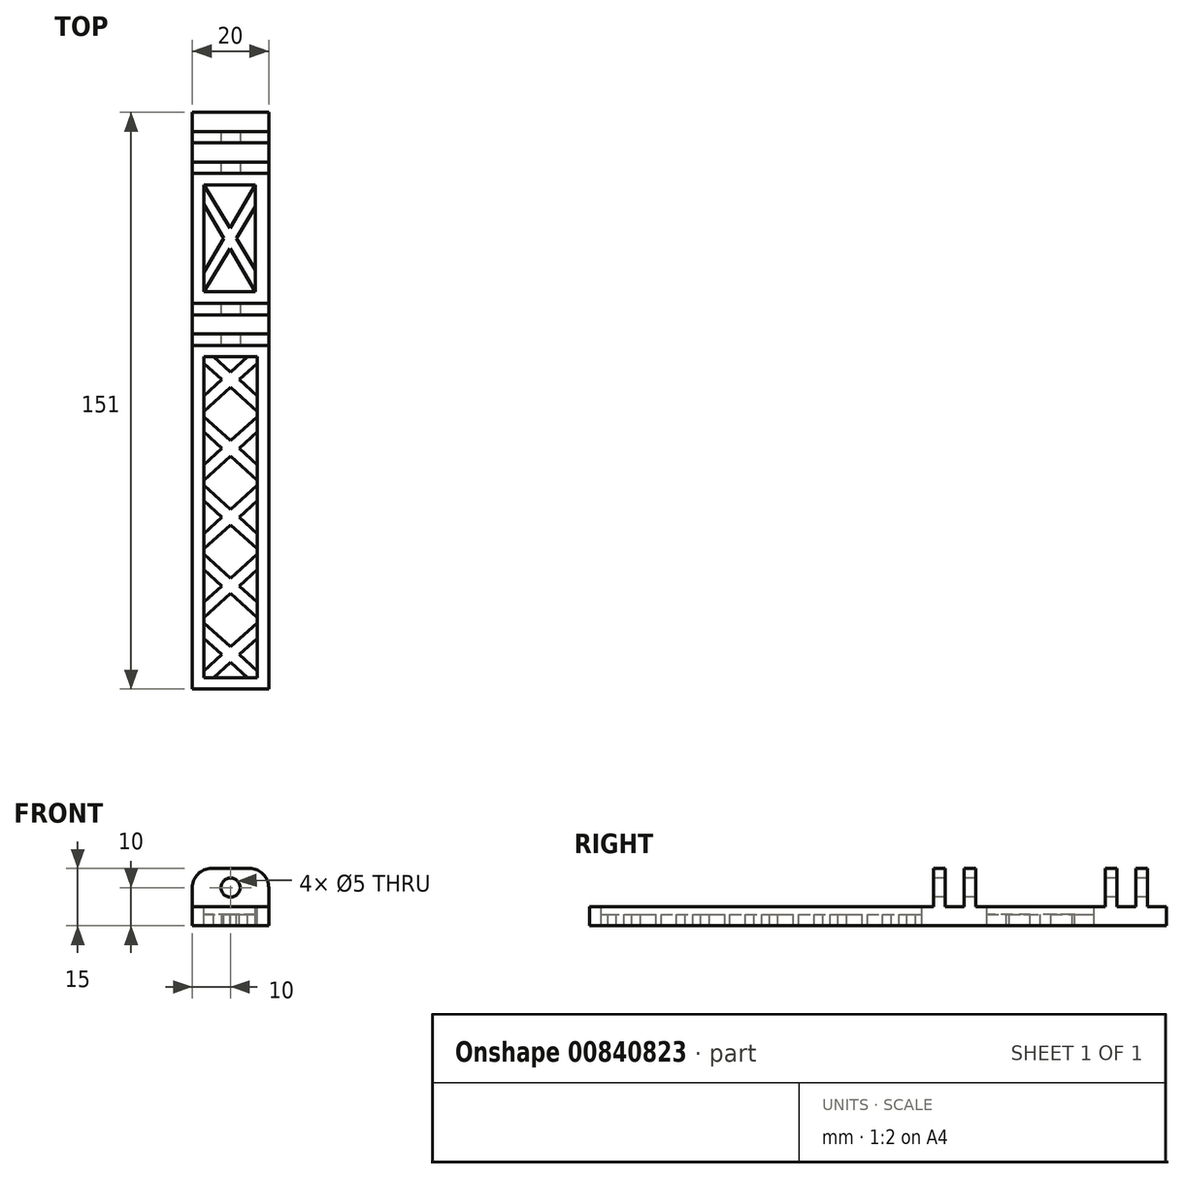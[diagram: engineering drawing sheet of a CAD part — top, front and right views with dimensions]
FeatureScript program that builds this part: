
annotation { "Feature Type Name" : "Feature", "Feature Type Description" : "" }
export const myFeature = defineFeature(function(context is Context, id is Id, definition is map)
    precondition{}
    {
        {
            var Q0;
            Q0=qCreatedBy(makeId("Top.planeOp"),FACE);
            var sketch = newSketch(context, id + "F0", { "sketchPlane" : qUnion([Q0])});
            skLineSegment(sketch, "E0.bottom", {"start": v(10, 75.5) * mm, "end": v(-10, 75.5) * mm});
            skLineSegment(sketch, "E0.top", {"start": v(10, -75.5) * mm, "end": v(-10, -75.5) * mm});
            skLineSegment(sketch, "E0.left", {"start": v(10, 75.5) * mm, "end": v(10, -75.5) * mm});
            skLineSegment(sketch, "E0.right", {"start": v(-10, 75.5) * mm, "end": v(-10, -75.5) * mm});
            skPoint(sketch, "E0.middle", {"position": v(0, 0) * mm});
            skLineSegment(sketch, "E1.bottom", {"start": v(-10, 70.5) * mm, "end": v(10, 70.5) * mm});
            skLineSegment(sketch, "E1.top", {"start": v(-10, 67.5) * mm, "end": v(10, 67.5) * mm});
            skLineSegment(sketch, "E1.left", {"start": v(-10, 70.5) * mm, "end": v(-10, 67.5) * mm});
            skLineSegment(sketch, "E1.right", {"start": v(10, 70.5) * mm, "end": v(10, 67.5) * mm});
            skLineSegment(sketch, "E2", {"start": v(-10, 62.5) * mm, "end": v(10, 62.5) * mm});
            skLineSegment(sketch, "E3", {"start": v(-10, 59.5) * mm, "end": v(10, 59.5) * mm});
            skLineSegment(sketch, "E4", {"start": v(-10, 22.5) * mm, "end": v(10, 22.5) * mm});
            skLineSegment(sketch, "E5", {"start": v(-10, 17.5) * mm, "end": v(10, 17.5) * mm});
            skLineSegment(sketch, "E6", {"start": v(-10, 25.5) * mm, "end": v(10, 25.5) * mm});
            skLineSegment(sketch, "E7", {"start": v(-10, 14.5) * mm, "end": v(10, 14.5) * mm});
            skSolve(sketch);
        }
        {
            var Q0;
            {var subQ0=sQuery(id+"F0.wireOp",EDGE,"E3");var subQ5=makeQuery(id+"F0.imprint","IMPRINT",EDGE,{"derivedFrom":subQ0});var subQ10=sQuery(id+"F0.wireOp",EDGE,"E1.top");var subQ12=sQuery(id+"F0.wireOp",EDGE,"E1.bottom");var subQ14=makeQuery(id+"F0.imprint","IMPRINT",EDGE,{"derivedFrom":subQ12});var subQ17=makeQuery(id+"F0.imprint","IMPRINT",EDGE,{"derivedFrom":subQ10});var subQ20=sQuery(id+"F0.wireOp",EDGE,"E5");var subQ25=makeQuery(id+"F0.imprint","IMPRINT",EDGE,{"derivedFrom":subQ20});var subQ26=sQuery(id+"F0.wireOp",EDGE,"E0.top");var subQ27=sQuery(id+"F0.wireOp",EDGE,"E4");var subQ29=makeQuery(id+"F0.imprint","IMPRINT",EDGE,{"derivedFrom":subQ27});var subQ31=sQuery(id+"F0.wireOp",EDGE,"E0.bottom");var subQ32=sQuery(id+"F0.wireOp",EDGE,"E2");var subQ35=makeQuery(id+"F0.imprint","IMPRINT",EDGE,{"derivedFrom":subQ32});Q0=qUnion([makeQuery(id+"F0.imprint","IMPRINT",FACE,{"disambiguationData":[TD([[subQ17,-1.0]])]}),makeQuery(id+"F0.imprint","IMPRINT",FACE,{"disambiguationData":[TD([[subQ35,-1.0]])]}),makeQuery(id+"F0.imprint","IMPRINT",FACE,{"disambiguationData":[TD([[makeQuery(id+"F0.imprint","IMPRINT",EDGE,{"derivedFrom":subQ31}),1.0]])]}),makeQuery(id+"F0.imprint","IMPRINT",FACE,{"disambiguationData":[TD([[subQ29,-1.0]])]}),makeQuery(id+"F0.imprint","IMPRINT",FACE,{"disambiguationData":[TD([[subQ29,1.0]])]}),makeQuery(id+"F0.imprint","IMPRINT",FACE,{"disambiguationData":[TD([[makeQuery(id+"F0.imprint","IMPRINT",EDGE,{"derivedFrom":subQ26}),-1.0]])]}),makeQuery(id+"F0.imprint","IMPRINT",FACE,{"disambiguationData":[TD([[subQ25,-1.0]])]}),makeQuery(id+"F0.imprint","IMPRINT",FACE,{"disambiguationData":[TD([[subQ14,-1.0]])]}),makeQuery(id+"F0.imprint","IMPRINT",FACE,{"disambiguationData":[TD([[subQ5,-1.0]])]})]);}
            extrude(context, id + "F1", {"entities" : qUnion([Q0]), "depth" : 5 * mm, "offsetDistance" : 25 * mm});
        }
        {
            var Q0;
            Q0=qCreatedBy(makeId("Top.planeOp"),FACE);
            var sketch = newSketch(context, id + "F2", { "sketchPlane" : qUnion([Q0])});
            skLineSegment(sketch, "E8.0", {"start": v(-10, 70.5) * mm, "end": v(10, 70.5) * mm});
            skLineSegment(sketch, "E9.0", {"start": v(-10, 67.5) * mm, "end": v(10, 67.5) * mm});
            skLineSegment(sketch, "E10.0", {"start": v(-10, 62.5) * mm, "end": v(10, 62.5) * mm});
            skLineSegment(sketch, "E11.0", {"start": v(-10, 59.5) * mm, "end": v(10, 59.5) * mm});
            skLineSegment(sketch, "E12.0", {"start": v(-10, 25.5) * mm, "end": v(10, 25.5) * mm});
            skLineSegment(sketch, "E13.0", {"start": v(-10, 22.5) * mm, "end": v(10, 22.5) * mm});
            skLineSegment(sketch, "E14.0", {"start": v(-10, 17.5) * mm, "end": v(10, 17.5) * mm});
            skLineSegment(sketch, "E15.0", {"start": v(-10, 14.5) * mm, "end": v(10, 14.5) * mm});
            skLineSegment(sketch, "E16.0", {"start": v(-10, 75.5) * mm, "end": v(-10, -75.5) * mm});
            skLineSegment(sketch, "E17.0", {"start": v(10, 75.5) * mm, "end": v(10, -75.5) * mm});
            skLineSegment(sketch, "E18.0.1", {"start": v(-10, -75.5) * mm, "end": v(10, -75.5) * mm});
            skLineSegment(sketch, "E18.0.2", {"start": v(10, -75.5) * mm, "end": v(10, 75.5) * mm});
            skLineSegment(sketch, "E18.0.3", {"start": v(10, 75.5) * mm, "end": v(-10, 75.5) * mm});
            skSolve(sketch);
        }
        {
            var Q0;
            {var subQ0=sQuery(id+"F2.wireOp",EDGE,"E8.0");var subQ1=sQuery(id+"F2.wireOp",EDGE,"E16.0");var subQ2=makeQuery(id+"F2.imprint","INTERSECT",VERTEX,{"derivedFrom":[subQ1,subQ0]});Q0=makeQuery(id+"F2.imprint","IMPRINT",FACE,{"disambiguationData":[TD([[makeQuery(id+"F2.imprint","IMPRINT",EDGE,{"disambiguationData":[TD([[subQ2,-1.0]])],"derivedFrom":subQ1}),1.0]])]});}
            var Q1;
            {var subQ0=sQuery(id+"F2.wireOp",EDGE,"E8.0");Q1=makeQuery(id+"F2.imprint","IMPRINT",FACE,{"disambiguationData":[TD([[makeQuery(id+"F2.imprint","IMPRINT",EDGE,{"derivedFrom":subQ0}),-1.0]])]});}
            var Q2;
            {var subQ0=sQuery(id+"F2.wireOp",EDGE,"E8.0");var subQ1=sQuery(id+"F2.wireOp",EDGE,"E18.0.2");var subQ2=makeQuery(id+"F2.imprint","INTERSECT",VERTEX,{"derivedFrom":[subQ1,subQ0]});Q2=makeQuery(id+"F2.imprint","IMPRINT",FACE,{"disambiguationData":[TD([[makeQuery(id+"F2.imprint","IMPRINT",EDGE,{"disambiguationData":[TD([[subQ2,-1.0]])],"derivedFrom":subQ1}),-1.0]])]});}
            var Q3;
            {var subQ0=sQuery(id+"F2.wireOp",EDGE,"E10.0");var subQ1=sQuery(id+"F2.wireOp",EDGE,"E18.0.2");var subQ2=makeQuery(id+"F2.imprint","INTERSECT",VERTEX,{"derivedFrom":[subQ1,subQ0]});Q3=makeQuery(id+"F2.imprint","IMPRINT",FACE,{"disambiguationData":[TD([[makeQuery(id+"F2.imprint","IMPRINT",EDGE,{"disambiguationData":[TD([[subQ2,-1.0]])],"derivedFrom":subQ1}),-1.0]])]});}
            var Q4;
            {var subQ0=sQuery(id+"F2.wireOp",EDGE,"E10.0");Q4=makeQuery(id+"F2.imprint","IMPRINT",FACE,{"disambiguationData":[TD([[makeQuery(id+"F2.imprint","IMPRINT",EDGE,{"derivedFrom":subQ0}),-1.0]])]});}
            var Q5;
            {var subQ0=sQuery(id+"F2.wireOp",EDGE,"E10.0");var subQ1=sQuery(id+"F2.wireOp",EDGE,"E16.0");var subQ2=makeQuery(id+"F2.imprint","INTERSECT",VERTEX,{"derivedFrom":[subQ1,subQ0]});Q5=makeQuery(id+"F2.imprint","IMPRINT",FACE,{"disambiguationData":[TD([[makeQuery(id+"F2.imprint","IMPRINT",EDGE,{"disambiguationData":[TD([[subQ2,-1.0]])],"derivedFrom":subQ1}),1.0]])]});}
            var Q6;
            {var subQ0=sQuery(id+"F2.wireOp",EDGE,"E12.0");var subQ1=sQuery(id+"F2.wireOp",EDGE,"E16.0");var subQ2=makeQuery(id+"F2.imprint","INTERSECT",VERTEX,{"derivedFrom":[subQ1,subQ0]});Q6=makeQuery(id+"F2.imprint","IMPRINT",FACE,{"disambiguationData":[TD([[makeQuery(id+"F2.imprint","IMPRINT",EDGE,{"disambiguationData":[TD([[subQ2,-1.0]])],"derivedFrom":subQ1}),1.0]])]});}
            var Q7;
            {var subQ0=sQuery(id+"F2.wireOp",EDGE,"E12.0");Q7=makeQuery(id+"F2.imprint","IMPRINT",FACE,{"disambiguationData":[TD([[makeQuery(id+"F2.imprint","IMPRINT",EDGE,{"derivedFrom":subQ0}),-1.0]])]});}
            var Q8;
            {var subQ0=sQuery(id+"F2.wireOp",EDGE,"E12.0");var subQ1=sQuery(id+"F2.wireOp",EDGE,"E18.0.2");var subQ2=makeQuery(id+"F2.imprint","INTERSECT",VERTEX,{"derivedFrom":[subQ1,subQ0]});Q8=makeQuery(id+"F2.imprint","IMPRINT",FACE,{"disambiguationData":[TD([[makeQuery(id+"F2.imprint","IMPRINT",EDGE,{"disambiguationData":[TD([[subQ2,-1.0]])],"derivedFrom":subQ1}),-1.0]])]});}
            var Q9;
            {var subQ0=sQuery(id+"F2.wireOp",EDGE,"E14.0");var subQ1=sQuery(id+"F2.wireOp",EDGE,"E18.0.2");var subQ2=makeQuery(id+"F2.imprint","INTERSECT",VERTEX,{"derivedFrom":[subQ1,subQ0]});Q9=makeQuery(id+"F2.imprint","IMPRINT",FACE,{"disambiguationData":[TD([[makeQuery(id+"F2.imprint","IMPRINT",EDGE,{"disambiguationData":[TD([[subQ2,-1.0]])],"derivedFrom":subQ1}),-1.0]])]});}
            var Q10;
            {var subQ0=sQuery(id+"F2.wireOp",EDGE,"E14.0");Q10=makeQuery(id+"F2.imprint","IMPRINT",FACE,{"disambiguationData":[TD([[makeQuery(id+"F2.imprint","IMPRINT",EDGE,{"derivedFrom":subQ0}),-1.0]])]});}
            var Q11;
            {var subQ0=sQuery(id+"F2.wireOp",EDGE,"E14.0");var subQ1=sQuery(id+"F2.wireOp",EDGE,"E16.0");var subQ2=makeQuery(id+"F2.imprint","INTERSECT",VERTEX,{"derivedFrom":[subQ1,subQ0]});Q11=makeQuery(id+"F2.imprint","IMPRINT",FACE,{"disambiguationData":[TD([[makeQuery(id+"F2.imprint","IMPRINT",EDGE,{"disambiguationData":[TD([[subQ2,-1.0]])],"derivedFrom":subQ1}),1.0]])]});}
            var Q12;
            Q12=makeQuery(id+"F1.opExtrude","CAP_FACE",FACE,{"disambiguationData":[OSD([sQuery(id+"F0.wireOp",EDGE,"E0.bottom"),sQuery(id+"F0.wireOp",EDGE,"E0.top"),sQuery(id+"F0.wireOp",EDGE,"E0.left"),sQuery(id+"F0.wireOp",EDGE,"E0.right")])],"isStart":false});
            extrude(context, id + "F3", {"entities" : qUnion([Q0, Q1, Q2, Q3, Q4, Q5, Q6, Q7, Q8, Q9, Q10, Q11]), "operationType" : NewBodyOperationType.ADD, "endBound" : BoundingType.UP_TO_SURFACE, "depth" : 10 * mm, "endBoundEntityFace" : qUnion([Q12]), "offsetDistance" : 25 * mm});
        }
        {
            var Q0;
            Q0=makeQuery(id+"F1.opExtrude","CAP_FACE",FACE,{"disambiguationData":[OSD([sQuery(id+"F0.wireOp",EDGE,"E0.bottom"),sQuery(id+"F0.wireOp",EDGE,"E0.top"),sQuery(id+"F0.wireOp",EDGE,"E0.left"),sQuery(id+"F0.wireOp",EDGE,"E0.right")])],"isStart":false});
            var sketch = newSketch(context, id + "F4", { "sketchPlane" : qUnion([Q0])});
            skPoint(sketch, "E19.0", {"position": v(-10, 70.5) * mm});
            skPoint(sketch, "E20.0", {"position": v(10, 67.5) * mm});
            skPoint(sketch, "E21.0", {"position": v(10, 62.5) * mm});
            skPoint(sketch, "E22.0", {"position": v(-10, 59.5) * mm});
            skPoint(sketch, "E23.0", {"position": v(-10, 25.5) * mm});
            skPoint(sketch, "E24.0", {"position": v(10, 22.5) * mm});
            skPoint(sketch, "E25.0", {"position": v(10, 17.5) * mm});
            skPoint(sketch, "E26.0", {"position": v(-10, 14.5) * mm});
            skLineSegment(sketch, "E27.bottom", {"start": v(-10, 70.5) * mm, "end": v(10, 70.5) * mm});
            skLineSegment(sketch, "E27.top", {"start": v(-10, 67.5) * mm, "end": v(10, 67.5) * mm});
            skLineSegment(sketch, "E27.left", {"start": v(-10, 70.5) * mm, "end": v(-10, 67.5) * mm});
            skLineSegment(sketch, "E27.right", {"start": v(10, 70.5) * mm, "end": v(10, 67.5) * mm});
            skLineSegment(sketch, "E28.bottom", {"start": v(10, 62.5) * mm, "end": v(-10, 62.5) * mm});
            skLineSegment(sketch, "E28.top", {"start": v(10, 59.5) * mm, "end": v(-10, 59.5) * mm});
            skLineSegment(sketch, "E28.left", {"start": v(10, 62.5) * mm, "end": v(10, 59.5) * mm});
            skLineSegment(sketch, "E28.right", {"start": v(-10, 62.5) * mm, "end": v(-10, 59.5) * mm});
            skLineSegment(sketch, "E29.bottom", {"start": v(-10, 25.5) * mm, "end": v(10, 25.5) * mm});
            skLineSegment(sketch, "E29.top", {"start": v(-10, 22.5) * mm, "end": v(10, 22.5) * mm});
            skLineSegment(sketch, "E29.left", {"start": v(-10, 25.5) * mm, "end": v(-10, 22.5) * mm});
            skLineSegment(sketch, "E29.right", {"start": v(10, 25.5) * mm, "end": v(10, 22.5) * mm});
            skLineSegment(sketch, "E30.bottom", {"start": v(10, 17.5) * mm, "end": v(-10, 17.5) * mm});
            skLineSegment(sketch, "E30.top", {"start": v(10, 14.5) * mm, "end": v(-10, 14.5) * mm});
            skLineSegment(sketch, "E30.left", {"start": v(10, 17.5) * mm, "end": v(10, 14.5) * mm});
            skLineSegment(sketch, "E30.right", {"start": v(-10, 17.5) * mm, "end": v(-10, 14.5) * mm});
            skSolve(sketch);
        }
        {
            var Q0;
            Q0 = qSketchRegion(id + "F4", true);
            extrude(context, id + "F5", {"entities" : qUnion([Q0]), "operationType" : NewBodyOperationType.ADD, "depth" : 10 * mm, "offsetDistance" : 25 * mm});
        }
        {
            var Q0;
            Q0=makeQuery(id+"F5.opExtrude","SWEPT_FACE",FACE,{"disambiguationData":[OSD([sQuery(id+"F4.wireOp",EDGE,"E30.top")])]});
            var sketch = newSketch(context, id + "F6", { "sketchPlane" : qUnion([Q0])});
            skCircle(sketch, "E31", {"center": v(0, 10) * mm, "radius": 2.5 * mm});
            skPoint(sketch, "E32", {"position": v(0, 15) * mm});
            skPoint(sketch, "E33", {"position": v(-10, 10) * mm});
            skSolve(sketch);
        }
        {
            var Q0;
            Q0=makeQuery(id+"F6.imprint","IMPRINT",FACE,{"disambiguationData":[TD([[makeQuery(id+"F6.imprint","IMPRINT",EDGE,{"derivedFrom":sQuery(id+"F6.wireOp",EDGE,"E31")}),1.0]])]});
            var Q1;
            Q1=makeQuery(id+"F5.opExtrude","SWEPT_FACE",FACE,{"disambiguationData":[OSD([sQuery(id+"F4.wireOp",EDGE,"E27.bottom")])]});
            extrude(context, id + "F7", {"entities" : qUnion([Q0]), "operationType" : NewBodyOperationType.REMOVE, "endBound" : BoundingType.UP_TO_SURFACE, "oppositeDirection" : true, "depth" : 25 * mm, "endBoundEntityFace" : qUnion([Q1]), "offsetDistance" : 25 * mm});
        }
        {
            var Q0;
            Q0=makeQuery(id+"F5.opExtrude","CAP_EDGE",EDGE,{"disambiguationData":[OSD([sQuery(id+"F4.wireOp",EDGE,"E27.right")])],"isStart":false});
            var Q1;
            Q1=makeQuery(id+"F5.opExtrude","CAP_EDGE",EDGE,{"disambiguationData":[OSD([sQuery(id+"F4.wireOp",EDGE,"E28.left")])],"isStart":false});
            var Q2;
            Q2=makeQuery(id+"F5.opExtrude","CAP_EDGE",EDGE,{"disambiguationData":[OSD([sQuery(id+"F4.wireOp",EDGE,"E28.right")])],"isStart":false});
            var Q3;
            Q3=makeQuery(id+"F5.opExtrude","CAP_EDGE",EDGE,{"disambiguationData":[OSD([sQuery(id+"F4.wireOp",EDGE,"E27.left")])],"isStart":false});
            var Q4;
            Q4=makeQuery(id+"F5.opExtrude","CAP_EDGE",EDGE,{"disambiguationData":[OSD([sQuery(id+"F4.wireOp",EDGE,"E29.right")])],"isStart":false});
            var Q5;
            Q5=makeQuery(id+"F5.opExtrude","CAP_EDGE",EDGE,{"disambiguationData":[OSD([sQuery(id+"F4.wireOp",EDGE,"E29.left")])],"isStart":false});
            var Q6;
            Q6=makeQuery(id+"F5.opExtrude","CAP_EDGE",EDGE,{"disambiguationData":[OSD([sQuery(id+"F4.wireOp",EDGE,"E30.right")])],"isStart":false});
            var Q7;
            Q7=makeQuery(id+"F5.opExtrude","CAP_EDGE",EDGE,{"disambiguationData":[OSD([sQuery(id+"F4.wireOp",EDGE,"E30.left")])],"isStart":false});
            fillet(context, id + "F8", {"entities" : qUnion([Q0, Q1, Q2, Q3, Q4, Q5, Q6, Q7]), "radius" : 5 * mm, "tangentPropagation" : true, "allowEdgeOverflow" : false});
        }
        {
            var Q0;
            {var subQ0=sQuery(id+"F0.wireOp",EDGE,"E0.right");var subQ1=sQuery(id+"F0.wireOp",EDGE,"E0.top");var subQ2=sQuery(id+"F0.wireOp",EDGE,"E0.left");Q0=makeQuery(id+"F5.boolean.opBoolean","SPLIT",FACE,{"disambiguationData":[TD([makeQuery(id+"F1.opExtrude","SWEPT_FACE",FACE,{"disambiguationData":[OSD([subQ1])]})])],"derivedFrom":makeQuery(id+"F1.opExtrude","CAP_FACE",FACE,{"disambiguationData":[OSD([sQuery(id+"F0.wireOp",EDGE,"E0.bottom"),subQ1,subQ2,subQ0])],"isStart":false})});}
            var sketch = newSketch(context, id + "F9", { "sketchPlane" : qUnion([Q0])});
            skLineSegment(sketch, "E34.bottom", {"start": v(-10, 14.5) * mm, "end": v(10, 14.5) * mm});
            skLineSegment(sketch, "E34.top", {"start": v(-10, -75.5) * mm, "end": v(10, -75.5) * mm});
            skLineSegment(sketch, "E34.left", {"start": v(-10, 14.5) * mm, "end": v(-10, -75.5) * mm});
            skLineSegment(sketch, "E34.right", {"start": v(10, 14.5) * mm, "end": v(10, -75.5) * mm});
            skLineSegment(sketch, "E35", {"start": v(-10, 14.5) * mm, "end": v(10, -3.5) * mm, "construction": true});
            skLineSegment(sketch, "E36", {"start": v(10, -3.5) * mm, "end": v(-10, -21.5) * mm, "construction": true});
            skLineSegment(sketch, "E37", {"start": v(-10, -21.5) * mm, "end": v(10, -39.5) * mm, "construction": true});
            skLineSegment(sketch, "E38", {"start": v(10, -39.5) * mm, "end": v(-10, -57.5) * mm, "construction": true});
            skLineSegment(sketch, "E39", {"start": v(-10, -57.5) * mm, "end": v(10, -75.5) * mm, "construction": true});
            skLineSegment(sketch, "E40.0", {"start": v(-11, 13.39) * mm, "end": v(9, -4.61) * mm});
            skLineSegment(sketch, "E41.MirrorCS", {"start": v(-9, 15.61) * mm, "end": v(11, -2.39) * mm});
            skLineSegment(sketch, "E42.0", {"start": v(9, -2.39) * mm, "end": v(-11, -20.39) * mm});
            skLineSegment(sketch, "E43.0", {"start": v(-9, -20.39) * mm, "end": v(11, -38.39) * mm});
            skLineSegment(sketch, "E44.0", {"start": v(9, -38.39) * mm, "end": v(-11, -56.39) * mm});
            skLineSegment(sketch, "E45.0", {"start": v(-11, -58.61) * mm, "end": v(9, -76.61) * mm});
            skLineSegment(sketch, "E46.MirrorCS", {"start": v(-11, -22.61) * mm, "end": v(9, -40.61) * mm});
            skLineSegment(sketch, "E47.MirrorCS", {"start": v(11, -40.61) * mm, "end": v(-9, -58.61) * mm});
            skLineSegment(sketch, "E48.MirrorCS", {"start": v(-9, -56.39) * mm, "end": v(11, -74.39) * mm});
            skLineSegment(sketch, "E49.0", {"start": v(-7, 14.5) * mm, "end": v(-7, -75.5) * mm});
            skLineSegment(sketch, "E50.0", {"start": v(-10, -72.5) * mm, "end": v(10, -72.5) * mm});
            skLineSegment(sketch, "E51.0", {"start": v(7, 14.5) * mm, "end": v(7, -75.5) * mm});
            skLineSegment(sketch, "E52.0", {"start": v(-10, 11.5) * mm, "end": v(10, 11.5) * mm});
            skPoint(sketch, "E53", {"position": v(-4.42, 11.5) * mm});
            skPoint(sketch, "E54", {"position": v(7, 1.22) * mm});
            skPoint(sketch, "E55", {"position": v(-7, 9.78) * mm});
            skLineSegment(sketch, "E56.MirrorCS", {"start": v(11, -4.61) * mm, "end": v(-9, -22.61) * mm});
            skPoint(sketch, "E57", {"position": v(7, -8.22) * mm});
            skPoint(sketch, "E58", {"position": v(-7, -26.22) * mm});
            skPoint(sketch, "E59", {"position": v(-7, -16.78) * mm});
            skPoint(sketch, "E60", {"position": v(7, -34.78) * mm});
            skPoint(sketch, "E61", {"position": v(7, -44.22) * mm});
            skPoint(sketch, "E62", {"position": v(-7, -52.78) * mm});
            skPoint(sketch, "E63", {"position": v(-7, -62.22) * mm});
            skPoint(sketch, "E64", {"position": v(4.42, -72.5) * mm});
            skPoint(sketch, "E65", {"position": v(7, -70.78) * mm});
            skLineSegment(sketch, "E66.MirrorCS", {"start": v(9, 15.61) * mm, "end": v(-11, -2.39) * mm});
            skLineSegment(sketch, "E67.MirrorCS", {"start": v(11, 13.39) * mm, "end": v(-9, -4.61) * mm});
            skLineSegment(sketch, "E68.MirrorCS", {"start": v(-9, -2.39) * mm, "end": v(11, -20.39) * mm});
            skLineSegment(sketch, "E69.MirrorCS", {"start": v(-11, -4.61) * mm, "end": v(9, -22.61) * mm});
            skLineSegment(sketch, "E70.MirrorCS", {"start": v(9, -20.39) * mm, "end": v(-11, -38.39) * mm});
            skLineSegment(sketch, "E71.MirrorCS", {"start": v(11, -22.61) * mm, "end": v(-9, -40.61) * mm});
            skLineSegment(sketch, "E72.MirrorCS", {"start": v(-9, -38.39) * mm, "end": v(11, -56.39) * mm});
            skLineSegment(sketch, "E73.MirrorCS", {"start": v(-11, -40.61) * mm, "end": v(9, -58.61) * mm});
            skLineSegment(sketch, "E74.MirrorCS", {"start": v(9, -56.39) * mm, "end": v(-11, -74.39) * mm});
            skLineSegment(sketch, "E75.MirrorCS", {"start": v(11, -58.61) * mm, "end": v(-9, -76.61) * mm});
            skSolve(sketch);
        }
        {
            var Q0;
            {var subQ0=sQuery(id+"F9.wireOp",EDGE,"E52.0");var subQ1=sQuery(id+"F9.wireOp",EDGE,"E41.MirrorCS");var subQ2=makeQuery(id+"F9.imprint","INTERSECT",VERTEX,{"derivedFrom":[subQ1,subQ0]});Q0=makeQuery(id+"F9.imprint","IMPRINT",FACE,{"disambiguationData":[TD([[makeQuery(id+"F9.imprint","IMPRINT",EDGE,{"disambiguationData":[TD([[subQ2,-1.0]])],"derivedFrom":subQ1}),1.0]])]});}
            var Q1;
            {var subQ0=sQuery(id+"F9.wireOp",EDGE,"E49.0");var subQ1=sQuery(id+"F9.wireOp",EDGE,"E40.0");var subQ2=makeQuery(id+"F9.imprint","INTERSECT",VERTEX,{"derivedFrom":[subQ1,subQ0]});Q1=makeQuery(id+"F9.imprint","IMPRINT",FACE,{"disambiguationData":[TD([[makeQuery(id+"F9.imprint","IMPRINT",EDGE,{"disambiguationData":[TD([[subQ2,-1.0]])],"derivedFrom":subQ1}),-1.0]])]});}
            var Q2;
            {var subQ0=sQuery(id+"F9.wireOp",EDGE,"E49.0");var subQ1=sQuery(id+"F9.wireOp",EDGE,"E43.0");var subQ2=makeQuery(id+"F9.imprint","INTERSECT",VERTEX,{"derivedFrom":[subQ1,subQ0]});Q2=makeQuery(id+"F9.imprint","IMPRINT",FACE,{"disambiguationData":[TD([[makeQuery(id+"F9.imprint","IMPRINT",EDGE,{"disambiguationData":[TD([[subQ2,-1.0]])],"derivedFrom":subQ1}),1.0]])]});}
            var Q3;
            {var subQ0=sQuery(id+"F9.wireOp",EDGE,"E51.0");var subQ1=sQuery(id+"F9.wireOp",EDGE,"E44.0");var subQ2=makeQuery(id+"F9.imprint","INTERSECT",VERTEX,{"derivedFrom":[subQ1,subQ0]});Q3=makeQuery(id+"F9.imprint","IMPRINT",FACE,{"disambiguationData":[TD([[makeQuery(id+"F9.imprint","IMPRINT",EDGE,{"disambiguationData":[TD([[subQ2,-1.0]])],"derivedFrom":subQ1}),-1.0]])]});}
            var Q4;
            {var subQ0=sQuery(id+"F9.wireOp",EDGE,"E51.0");var subQ1=sQuery(id+"F9.wireOp",EDGE,"E47.MirrorCS");var subQ2=makeQuery(id+"F9.imprint","INTERSECT",VERTEX,{"derivedFrom":[subQ1,subQ0]});Q4=makeQuery(id+"F9.imprint","IMPRINT",FACE,{"disambiguationData":[TD([[makeQuery(id+"F9.imprint","IMPRINT",EDGE,{"disambiguationData":[TD([[subQ2,-1.0]])],"derivedFrom":subQ1}),1.0]])]});}
            var Q5;
            {var subQ0=sQuery(id+"F9.wireOp",EDGE,"E49.0");var subQ1=sQuery(id+"F9.wireOp",EDGE,"E45.0");var subQ2=makeQuery(id+"F9.imprint","INTERSECT",VERTEX,{"derivedFrom":[subQ1,subQ0]});Q5=makeQuery(id+"F9.imprint","IMPRINT",FACE,{"disambiguationData":[TD([[makeQuery(id+"F9.imprint","IMPRINT",EDGE,{"disambiguationData":[TD([[subQ2,-1.0]])],"derivedFrom":subQ1}),-1.0]])]});}
            var Q6;
            {var subQ5=sQuery(id+"F9.wireOp",EDGE,"E40.0");var subQ7=sQuery(id+"F9.wireOp",EDGE,"E67.MirrorCS");var subQ11=makeQuery(id+"F9.imprint","INTERSECT",VERTEX,{"derivedFrom":[subQ5,subQ7]});Q6=makeQuery(id+"F9.imprint","IMPRINT",FACE,{"disambiguationData":[TD([[makeQuery(id+"F9.imprint","IMPRINT",EDGE,{"disambiguationData":[TD([[subQ11,-1.0]])],"derivedFrom":subQ5}),-1.0]])]});}
            var Q7;
            {var subQ0=sQuery(id+"F9.wireOp",EDGE,"E67.MirrorCS");var subQ1=sQuery(id+"F9.wireOp",EDGE,"E41.MirrorCS");var subQ2=makeQuery(id+"F9.imprint","INTERSECT",VERTEX,{"derivedFrom":[subQ1,subQ0]});Q7=makeQuery(id+"F9.imprint","IMPRINT",FACE,{"disambiguationData":[TD([[makeQuery(id+"F9.imprint","IMPRINT",EDGE,{"disambiguationData":[TD([[subQ2,-1.0]])],"derivedFrom":subQ1}),1.0]])]});}
            var Q8;
            {var subQ0=sQuery(id+"F9.wireOp",EDGE,"E56.MirrorCS");var subQ1=sQuery(id+"F9.wireOp",EDGE,"E51.0");var subQ2=makeQuery(id+"F9.imprint","INTERSECT",VERTEX,{"derivedFrom":[subQ1,subQ0]});Q8=makeQuery(id+"F9.imprint","IMPRINT",FACE,{"disambiguationData":[TD([[makeQuery(id+"F9.imprint","IMPRINT",EDGE,{"disambiguationData":[TD([[subQ2,-1.0]])],"derivedFrom":subQ1}),-1.0]])]});}
            var Q9;
            {var subQ0=sQuery(id+"F9.wireOp",EDGE,"E69.MirrorCS");var subQ1=sQuery(id+"F9.wireOp",EDGE,"E42.0");var subQ2=makeQuery(id+"F9.imprint","INTERSECT",VERTEX,{"derivedFrom":[subQ1,subQ0]});Q9=makeQuery(id+"F9.imprint","IMPRINT",FACE,{"disambiguationData":[TD([[makeQuery(id+"F9.imprint","IMPRINT",EDGE,{"disambiguationData":[TD([[subQ2,-1.0]])],"derivedFrom":subQ1}),-1.0]])]});}
            var Q10;
            {var subQ0=sQuery(id+"F9.wireOp",EDGE,"E71.MirrorCS");var subQ1=sQuery(id+"F9.wireOp",EDGE,"E43.0");var subQ2=makeQuery(id+"F9.imprint","INTERSECT",VERTEX,{"derivedFrom":[subQ1,subQ0]});Q10=makeQuery(id+"F9.imprint","IMPRINT",FACE,{"disambiguationData":[TD([[makeQuery(id+"F9.imprint","IMPRINT",EDGE,{"disambiguationData":[TD([[subQ2,-1.0]])],"derivedFrom":subQ1}),1.0]])]});}
            var Q11;
            {var subQ0=sQuery(id+"F9.wireOp",EDGE,"E49.0");var subQ1=sQuery(id+"F9.wireOp",EDGE,"E46.MirrorCS");var subQ2=makeQuery(id+"F9.imprint","INTERSECT",VERTEX,{"derivedFrom":[subQ1,subQ0]});Q11=makeQuery(id+"F9.imprint","IMPRINT",FACE,{"disambiguationData":[TD([[makeQuery(id+"F9.imprint","IMPRINT",EDGE,{"disambiguationData":[TD([[subQ2,-1.0]])],"derivedFrom":subQ1}),-1.0]])]});}
            var Q12;
            {var subQ0=sQuery(id+"F9.wireOp",EDGE,"E73.MirrorCS");var subQ1=sQuery(id+"F9.wireOp",EDGE,"E44.0");var subQ2=makeQuery(id+"F9.imprint","INTERSECT",VERTEX,{"derivedFrom":[subQ1,subQ0]});Q12=makeQuery(id+"F9.imprint","IMPRINT",FACE,{"disambiguationData":[TD([[makeQuery(id+"F9.imprint","IMPRINT",EDGE,{"disambiguationData":[TD([[subQ2,-1.0]])],"derivedFrom":subQ1}),-1.0]])]});}
            var Q13;
            {var subQ5=sQuery(id+"F9.wireOp",EDGE,"E47.MirrorCS");var subQ7=sQuery(id+"F9.wireOp",EDGE,"E73.MirrorCS");var subQ8=makeQuery(id+"F9.imprint","INTERSECT",VERTEX,{"derivedFrom":[subQ5,subQ7]});Q13=makeQuery(id+"F9.imprint","IMPRINT",FACE,{"disambiguationData":[TD([[makeQuery(id+"F9.imprint","IMPRINT",EDGE,{"disambiguationData":[TD([[subQ8,-1.0]])],"derivedFrom":subQ5}),1.0]])]});}
            var Q14;
            {var subQ0=sQuery(id+"F9.wireOp",EDGE,"E75.MirrorCS");var subQ1=sQuery(id+"F9.wireOp",EDGE,"E48.MirrorCS");var subQ2=makeQuery(id+"F9.imprint","INTERSECT",VERTEX,{"derivedFrom":[subQ1,subQ0]});Q14=makeQuery(id+"F9.imprint","IMPRINT",FACE,{"disambiguationData":[TD([[makeQuery(id+"F9.imprint","IMPRINT",EDGE,{"disambiguationData":[TD([[subQ2,-1.0]])],"derivedFrom":subQ1}),1.0]])]});}
            var Q15;
            {var subQ0=sQuery(id+"F9.wireOp",EDGE,"E75.MirrorCS");var subQ1=sQuery(id+"F9.wireOp",EDGE,"E45.0");var subQ2=makeQuery(id+"F9.imprint","INTERSECT",VERTEX,{"derivedFrom":[subQ1,subQ0]});Q15=makeQuery(id+"F9.imprint","IMPRINT",FACE,{"disambiguationData":[TD([[makeQuery(id+"F9.imprint","IMPRINT",EDGE,{"disambiguationData":[TD([[subQ2,-1.0]])],"derivedFrom":subQ1}),-1.0]])]});}
            var Q16;
            Q16=makeQuery(id+"F1.opExtrude","CAP_FACE",FACE,{"disambiguationData":[OSD([sQuery(id+"F0.wireOp",EDGE,"E0.bottom"),sQuery(id+"F0.wireOp",EDGE,"E0.top"),sQuery(id+"F0.wireOp",EDGE,"E0.left"),sQuery(id+"F0.wireOp",EDGE,"E0.right")])],"isStart":true});
            extrude(context, id + "F10", {"entities" : qUnion([Q0, Q1, Q2, Q3, Q4, Q5, Q6, Q7, Q8, Q9, Q10, Q11, Q12, Q13, Q14, Q15]), "operationType" : NewBodyOperationType.REMOVE, "endBound" : BoundingType.UP_TO_SURFACE, "oppositeDirection" : true, "depth" : 25 * mm, "endBoundEntityFace" : qUnion([Q16]), "offsetDistance" : 25 * mm});
        }
        {
            var Q0;
            {var subQ0=sQuery(id+"F0.wireOp",EDGE,"E0.left");var subQ1=sQuery(id+"F0.wireOp",EDGE,"E0.right");Q0=makeQuery(id+"F5.boolean.opBoolean","SPLIT",FACE,{"disambiguationData":[TD([makeQuery(id+"F5.opExtrude","SWEPT_FACE",FACE,{"disambiguationData":[OSD([sQuery(id+"F4.wireOp",EDGE,"E28.top")])]})])],"derivedFrom":makeQuery(id+"F1.opExtrude","CAP_FACE",FACE,{"disambiguationData":[OSD([sQuery(id+"F0.wireOp",EDGE,"E0.bottom"),sQuery(id+"F0.wireOp",EDGE,"E0.top"),subQ0,subQ1])],"isStart":false})});}
            var sketch = newSketch(context, id + "F11", { "sketchPlane" : qUnion([Q0])});
            skLineSegment(sketch, "E76.0", {"start": v(8.7, 60.26) * mm, "end": v(-11.3, 26.26) * mm});
            skLineSegment(sketch, "E77.0", {"start": v(-10, 56.5) * mm, "end": v(10, 56.5) * mm});
            skLineSegment(sketch, "E78.0", {"start": v(-10, 28.5) * mm, "end": v(10, 28.5) * mm});
            skLineSegment(sketch, "E79.0", {"start": v(10, 75.5) * mm, "end": v(10, 56.54) * mm});
            skLineSegment(sketch, "E80.0", {"start": v(-10, 75.5) * mm, "end": v(-10, 56.5) * mm});
            skLineSegment(sketch, "E81", {"start": v(10, 56.54) * mm, "end": v(10, 28.5) * mm});
            skLineSegment(sketch, "E82", {"start": v(10, 28.5) * mm, "end": v(10, -75.5) * mm});
            skLineSegment(sketch, "E83", {"start": v(-10, 28.46) * mm, "end": v(-10, -75.5) * mm});
            skLineSegment(sketch, "E84", {"start": v(-10, 56.5) * mm, "end": v(-10, 28.46) * mm});
            skLineSegment(sketch, "E85.0", {"start": v(-7, 56.5) * mm, "end": v(-7, 28.46) * mm});
            skLineSegment(sketch, "E86.0", {"start": v(6.5, 56.54) * mm, "end": v(6.5, 28.5) * mm});
            skLineSegment(sketch, "E87", {"start": v(-7, 28.46) * mm, "end": v(10, 56.54) * mm});
            skLineSegment(sketch, "E88", {"start": v(6.5, 28.5) * mm, "end": v(-10, 56.5) * mm});
            skLineSegment(sketch, "E89", {"start": v(-7, 56.5) * mm, "end": v(10, 28.5) * mm});
            skSolve(sketch);
        }
        {
            var Q0;
            {var subQ0=sQuery(id+"F11.wireOp",EDGE,"E77.0");var subQ1=sQuery(id+"F11.wireOp",EDGE,"E76.0");var subQ2=makeQuery(id+"F11.imprint","INTERSECT",VERTEX,{"derivedFrom":[subQ1,subQ0]});Q0=makeQuery(id+"F11.imprint","IMPRINT",FACE,{"disambiguationData":[TD([[makeQuery(id+"F11.imprint","IMPRINT",EDGE,{"disambiguationData":[TD([[subQ2,-1.0]])],"derivedFrom":subQ1}),-1.0]])]});}
            var Q1;
            {var subQ0=sQuery(id+"F11.wireOp",EDGE,"E87");var subQ1=sQuery(id+"F11.wireOp",EDGE,"E86.0");var subQ2=makeQuery(id+"F11.imprint","INTERSECT",VERTEX,{"derivedFrom":[subQ1,subQ0]});Q1=makeQuery(id+"F11.imprint","IMPRINT",FACE,{"disambiguationData":[TD([[makeQuery(id+"F11.imprint","IMPRINT",EDGE,{"disambiguationData":[TD([[subQ2,-1.0]])],"derivedFrom":subQ1}),-1.0]])]});}
            var Q2;
            {var subQ1=sQuery(id+"F11.wireOp",EDGE,"E78.0");var subQ3=sQuery(id+"F11.wireOp",EDGE,"E87");var subQ4=makeQuery(id+"F11.imprint","INTERSECT",VERTEX,{"derivedFrom":[subQ1,subQ3]});Q2=makeQuery(id+"F11.imprint","IMPRINT",FACE,{"disambiguationData":[TD([[makeQuery(id+"F11.imprint","IMPRINT",EDGE,{"disambiguationData":[TD([[subQ4,-1.0]])],"derivedFrom":subQ3}),-1.0]])]});}
            var Q3;
            {var subQ0=sQuery(id+"F11.wireOp",EDGE,"E88");var subQ1=sQuery(id+"F11.wireOp",EDGE,"E76.0");var subQ2=makeQuery(id+"F11.imprint","INTERSECT",VERTEX,{"derivedFrom":[subQ1,subQ0]});Q3=makeQuery(id+"F11.imprint","IMPRINT",FACE,{"disambiguationData":[TD([[makeQuery(id+"F11.imprint","IMPRINT",EDGE,{"disambiguationData":[TD([[subQ2,-1.0]])],"derivedFrom":subQ1}),-1.0]])]});}
            var Q4;
            Q4=makeQuery(id+"F1.opExtrude","CAP_FACE",FACE,{"disambiguationData":[OSD([sQuery(id+"F0.wireOp",EDGE,"E0.bottom"),sQuery(id+"F0.wireOp",EDGE,"E0.top"),sQuery(id+"F0.wireOp",EDGE,"E0.left"),sQuery(id+"F0.wireOp",EDGE,"E0.right")])],"isStart":true});
            extrude(context, id + "F12", {"entities" : qUnion([Q0, Q1, Q2, Q3]), "operationType" : NewBodyOperationType.REMOVE, "endBound" : BoundingType.UP_TO_SURFACE, "oppositeDirection" : true, "depth" : 25 * mm, "endBoundEntityFace" : qUnion([Q4]), "offsetDistance" : 25 * mm});
        }
        {
            var Q0;
            {var subQ0=sQuery(id+"F0.wireOp",EDGE,"E0.left");var subQ1=sQuery(id+"F0.wireOp",EDGE,"E0.right");Q0=makeQuery(id+"F5.boolean.opBoolean","SPLIT",FACE,{"disambiguationData":[TD([makeQuery(id+"F5.opExtrude","SWEPT_FACE",FACE,{"disambiguationData":[OSD([sQuery(id+"F4.wireOp",EDGE,"E29.top")])]})])],"derivedFrom":makeQuery(id+"F1.opExtrude","CAP_FACE",FACE,{"disambiguationData":[OSD([sQuery(id+"F0.wireOp",EDGE,"E0.bottom"),sQuery(id+"F0.wireOp",EDGE,"E0.top"),subQ0,subQ1])],"isStart":false})});}
            var sketch = newSketch(context, id + "F13", { "sketchPlane" : qUnion([Q0])});
            skLineSegment(sketch, "E90.0", {"start": v(-10, 11.5) * mm, "end": v(10, 11.5) * mm});
            skLineSegment(sketch, "E91.0", {"start": v(-7, 14.5) * mm, "end": v(-7, -75.5) * mm});
            skLineSegment(sketch, "E92.0", {"start": v(7, 14.5) * mm, "end": v(7, -75.5) * mm});
            skLineSegment(sketch, "E93.0", {"start": v(-10, -72.5) * mm, "end": v(10, -72.5) * mm});
            skPoint(sketch, "E94", {"position": v(-7, 11.5) * mm});
            skPoint(sketch, "E95", {"position": v(7, 11.5) * mm});
            skPoint(sketch, "E96", {"position": v(7, -72.5) * mm});
            skPoint(sketch, "E97", {"position": v(-7, -72.5) * mm});
            skLineSegment(sketch, "E98.0", {"start": v(6.5, 56.54) * mm, "end": v(6.5, 28.5) * mm});
            skLineSegment(sketch, "E99.0", {"start": v(-7, 56.5) * mm, "end": v(-7, 28.46) * mm});
            skLineSegment(sketch, "E100.0", {"start": v(-10, 56.5) * mm, "end": v(10, 56.5) * mm});
            skLineSegment(sketch, "E101.0", {"start": v(-10, 28.5) * mm, "end": v(10, 28.5) * mm});
            skSolve(sketch);
        }
        {
            var Q0;
            Q0 = qSketchRegion(id + "F13", true);
            var Q1;
            Q1=makeQuery(id+"F1.opExtrude","CAP_FACE",FACE,{"disambiguationData":[OSD([sQuery(id+"F0.wireOp",EDGE,"E0.bottom"),sQuery(id+"F0.wireOp",EDGE,"E0.top"),sQuery(id+"F0.wireOp",EDGE,"E0.left"),sQuery(id+"F0.wireOp",EDGE,"E0.right")])],"isStart":true});
            extrude(context, id + "F14", {"entities" : qUnion([Q0]), "operationType" : NewBodyOperationType.REMOVE, "endBound" : BoundingType.UP_TO_SURFACE, "oppositeDirection" : true, "depth" : 3 * mm, "endBoundEntityFace" : qUnion([Q1]), "hasOffset" : true, "offsetDistance" : 3 * mm});
        }
    });
